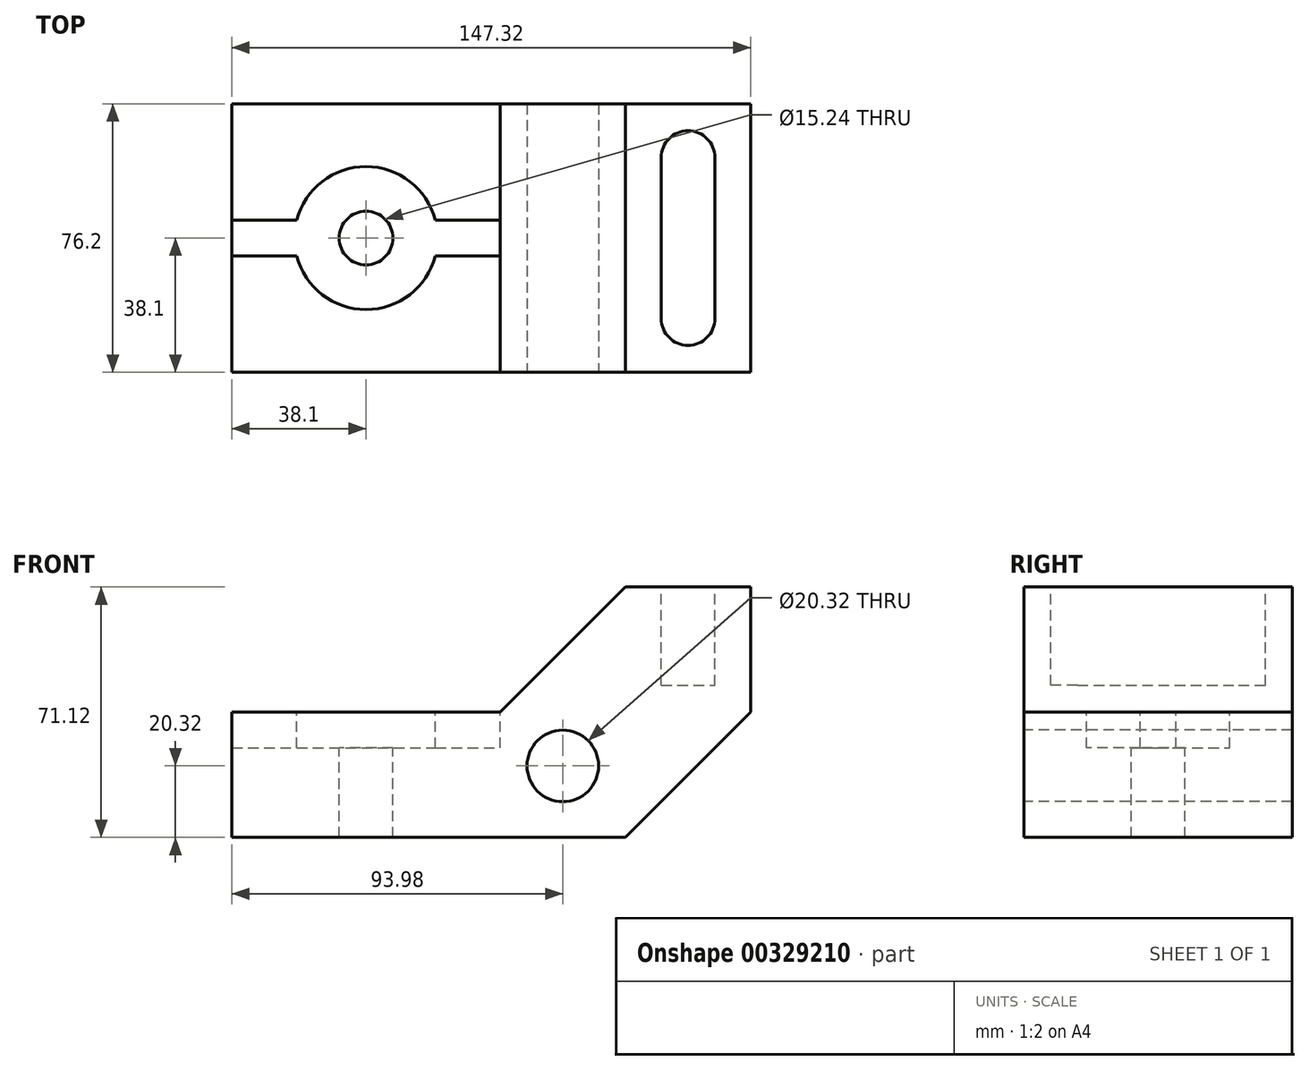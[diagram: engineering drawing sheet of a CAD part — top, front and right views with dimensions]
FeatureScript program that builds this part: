
annotation { "Feature Type Name" : "Feature", "Feature Type Description" : "" }
export const myFeature = defineFeature(function(context is Context, id is Id, definition is map)
    precondition{}
    {
        {
            var Q0;
            Q0=qCreatedBy(makeId("Front.planeOp"),FACE);
            var sketch = newSketch(context, id + "F0", { "sketchPlane" : qUnion([Q0])});
            skLineSegment(sketch, "E0", {"start": v(0, 0) * mm, "end": v(111.76, 0) * mm});
            skLineSegment(sketch, "E1", {"start": v(111.76, 0) * mm, "end": v(147.32, 35.56) * mm});
            skLineSegment(sketch, "E2", {"start": v(147.32, 35.56) * mm, "end": v(147.32, 71.12) * mm});
            skLineSegment(sketch, "E3", {"start": v(147.32, 71.12) * mm, "end": v(111.76, 71.12) * mm});
            skLineSegment(sketch, "E4", {"start": v(111.76, 71.12) * mm, "end": v(76.2, 35.56) * mm});
            skLineSegment(sketch, "E5", {"start": v(76.2, 35.56) * mm, "end": v(0, 35.56) * mm});
            skLineSegment(sketch, "E6", {"start": v(0, 35.56) * mm, "end": v(0, 0) * mm});
            skSolve(sketch);
        }
        {
            var Q0;
            Q0 = qSketchRegion(id + "F0", true);
            extrude(context, id + "F1", {"entities" : qUnion([Q0]), "depth" : 76.2 * mm});
        }
        {
            var Q0;
            Q0=makeQuery(id+"F1.opExtrude","SWEPT_FACE",FACE,{"disambiguationData":[OSD([sQuery(id+"F0.wireOp",EDGE,"E5")])]});
            var sketch = newSketch(context, id + "F2", { "sketchPlane" : qUnion([Q0])});
            skPoint(sketch, "E7", {"position": v(38.1, -38.1) * mm});
            skPoint(sketch, "E7.positionSnap0", {"position": v(38.1, 0) * mm});
            skSolve(sketch);
        }
        {
            var Q0;
            Q0=sQuery(id+"F2.wireOp",VERTEX,"E7");
            var Q1;
            Q1=makeQuery(id+"F1.opExtrude","SWEPT_BODY",BODY,{"disambiguationData":[OSD([sQuery(id+"F0.wireOp",EDGE,"E0"),sQuery(id+"F0.wireOp",EDGE,"E1"),sQuery(id+"F0.wireOp",EDGE,"E2"),sQuery(id+"F0.wireOp",EDGE,"E3"),sQuery(id+"F0.wireOp",EDGE,"E4"),sQuery(id+"F0.wireOp",EDGE,"E5"),sQuery(id+"F0.wireOp",EDGE,"E6")])]});
            hole(context, id + "F3", {"style" : HoleStyle.C_BORE, "endStyle" : HoleEndStyle.THROUGH, "holeDiameter" : 15.24 * mm, "cBoreDiameter" : 40.64 * mm, "cBoreDepth" : 10.16 * mm, "tappedDepth" : 12.7 * mm, "tapClearance" : 3, "locations" : qUnion([Q0]), "scope" : qUnion([Q1])});
        }
        {
            var Q0;
            Q0=makeQuery(id+"F1.opExtrude","CAP_FACE",FACE,{"disambiguationData":[OSD([sQuery(id+"F0.wireOp",EDGE,"E0"),sQuery(id+"F0.wireOp",EDGE,"E1"),sQuery(id+"F0.wireOp",EDGE,"E2"),sQuery(id+"F0.wireOp",EDGE,"E3"),sQuery(id+"F0.wireOp",EDGE,"E4"),sQuery(id+"F0.wireOp",EDGE,"E5"),sQuery(id+"F0.wireOp",EDGE,"E6")])],"isStart":false});
            var sketch = newSketch(context, id + "F4", { "sketchPlane" : qUnion([Q0])});
            skPoint(sketch, "E8", {"position": v(93.98, 20.32) * mm});
            skSolve(sketch);
        }
        {
            var Q0;
            Q0=sQuery(id+"F4.wireOp",VERTEX,"E8");
            var Q1;
            Q1=makeQuery(id+"F1.opExtrude","SWEPT_BODY",BODY,{"disambiguationData":[OSD([sQuery(id+"F0.wireOp",EDGE,"E0"),sQuery(id+"F0.wireOp",EDGE,"E1"),sQuery(id+"F0.wireOp",EDGE,"E2"),sQuery(id+"F0.wireOp",EDGE,"E3"),sQuery(id+"F0.wireOp",EDGE,"E4"),sQuery(id+"F0.wireOp",EDGE,"E5"),sQuery(id+"F0.wireOp",EDGE,"E6")])]});
            hole(context, id + "F5", {"style" : HoleStyle.SIMPLE, "endStyle" : HoleEndStyle.THROUGH, "holeDiameter" : 20.32 * mm, "tappedDepth" : 12.7 * mm, "tapClearance" : 3, "locations" : qUnion([Q0]), "scope" : qUnion([Q1])});
        }
        {
            var Q0;
            Q0=makeQuery(id+"F1.opExtrude","SWEPT_FACE",FACE,{"disambiguationData":[OSD([sQuery(id+"F0.wireOp",EDGE,"E3")])]});
            var sketch = newSketch(context, id + "F6", { "sketchPlane" : qUnion([Q0])});
            skPoint(sketch, "E9", {"position": v(129.54, -15.24) * mm});
            skPoint(sketch, "E10", {"position": v(129.54, -60.96) * mm});
            skArc(sketch, "E11", {"start": v(137.16, -15.24) * mm, "mid": v(129.54, -7.62) * mm, "end": v(121.92, -15.24) * mm});
            skArc(sketch, "E12", {"start": v(121.92, -60.96) * mm, "mid": v(129.54, -68.58) * mm, "end": v(137.16, -60.96) * mm});
            skLineSegment(sketch, "E13", {"start": v(137.16, -60.96) * mm, "end": v(137.16, -15.24) * mm});
            skLineSegment(sketch, "E14", {"start": v(121.92, -60.96) * mm, "end": v(121.92, -15.24) * mm});
            skSolve(sketch);
        }
        {
            var Q0;
            Q0 = qSketchRegion(id + "F6", true);
            extrude(context, id + "F7", {"entities" : qUnion([Q0]), "operationType" : NewBodyOperationType.REMOVE, "oppositeDirection" : true, "depth" : 27.94 * mm});
        }
        {
            var Q0;
            Q0=makeQuery(id+"F1.opExtrude","SWEPT_FACE",FACE,{"disambiguationData":[OSD([sQuery(id+"F0.wireOp",EDGE,"E5")])]});
            var sketch = newSketch(context, id + "F8", { "sketchPlane" : qUnion([Q0])});
            skLineSegment(sketch, "E15", {"start": v(0, -33.02) * mm, "end": v(76.2, -33.02) * mm});
            skLineSegment(sketch, "E16", {"start": v(0, -43.18) * mm, "end": v(76.2, -43.18) * mm});
            skPoint(sketch, "E17", {"position": v(38.1, -38.1) * mm});
            skSolve(sketch);
        }
        {
            var Q0;
            {var subQ0=sQuery(id+"F8.wireOp",EDGE,"E15");var subQ1=makeQuery(id+"F1.opExtrude","SWEPT_EDGE",EDGE,{"disambiguationData":[OSD([sQuery(id+"F0.wireOp",EDGE,"E5"),sQuery(id+"F0.wireOp",EDGE,"E6")])]});var subQ2=makeQuery(id+"F8.imprint","INTERSECT",VERTEX,{"derivedFrom":[subQ1,subQ0]});Q0=makeQuery(id+"F8.imprint","IMPRINT",FACE,{"disambiguationData":[TD([[makeQuery(id+"F8.imprint","IMPRINT",EDGE,{"disambiguationData":[TD([[subQ2,-1.0]])],"derivedFrom":subQ0}),-1.0]])]});}
            var Q1;
            {var subQ0=sQuery(id+"F8.wireOp",EDGE,"E15");var subQ1=makeQuery(id+"F1.opExtrude","SWEPT_EDGE",EDGE,{"disambiguationData":[OSD([sQuery(id+"F0.wireOp",EDGE,"E4"),sQuery(id+"F0.wireOp",EDGE,"E5")])]});var subQ2=makeQuery(id+"F8.imprint","INTERSECT",VERTEX,{"derivedFrom":[subQ1,subQ0]});Q1=makeQuery(id+"F8.imprint","IMPRINT",FACE,{"disambiguationData":[TD([[makeQuery(id+"F8.imprint","IMPRINT",EDGE,{"disambiguationData":[TD([[subQ2,1.0]])],"derivedFrom":subQ0}),-1.0]])]});}
            extrude(context, id + "F9", {"entities" : qUnion([Q0, Q1]), "operationType" : NewBodyOperationType.REMOVE, "oppositeDirection" : true, "depth" : 10.16 * mm});
        }
    });
